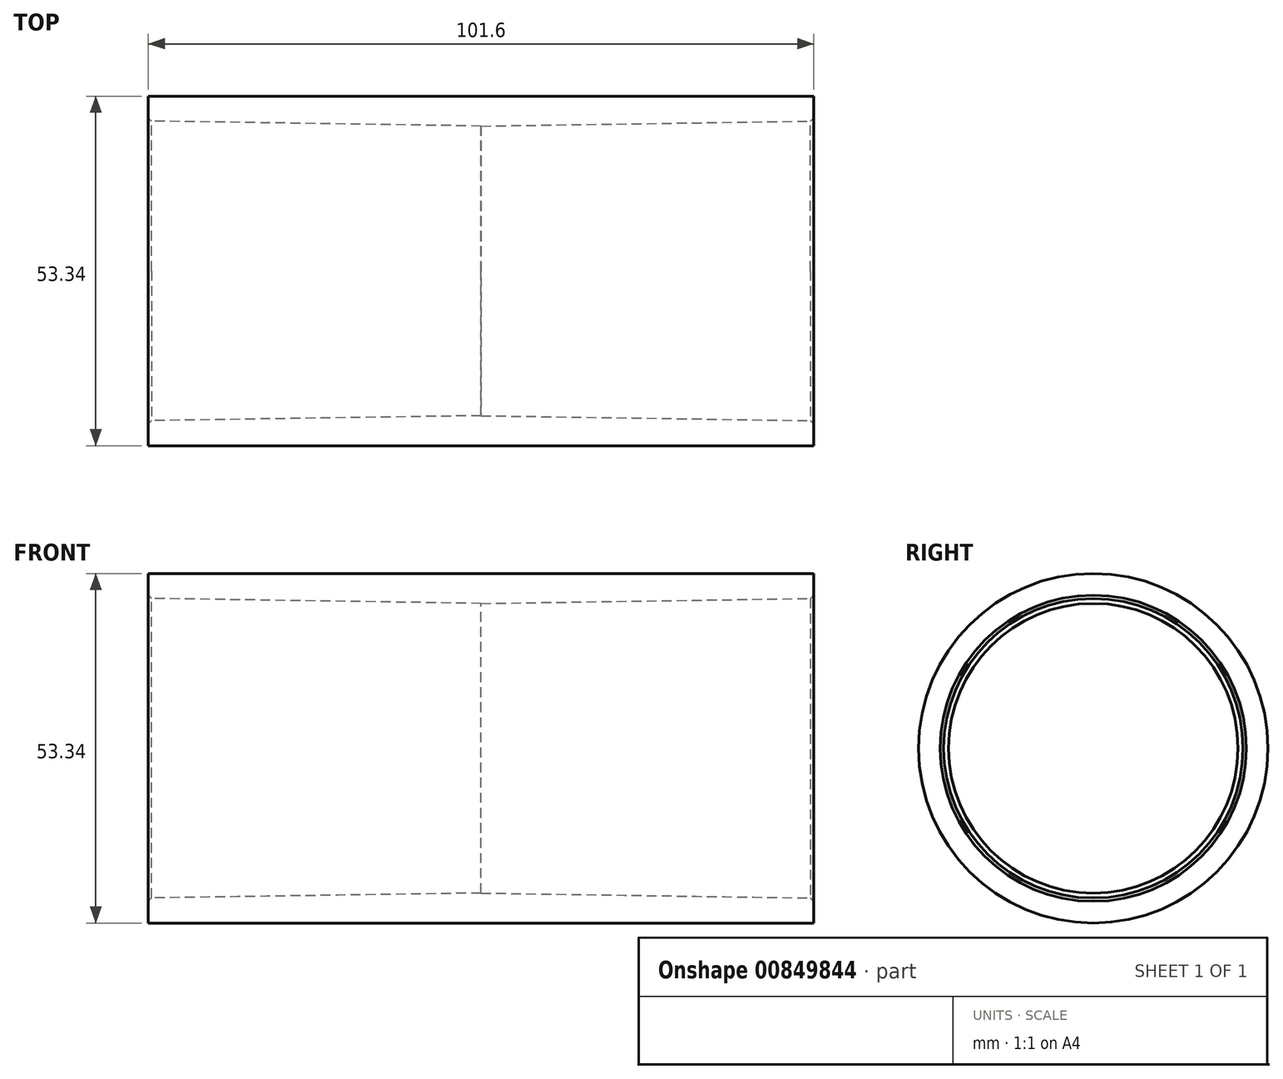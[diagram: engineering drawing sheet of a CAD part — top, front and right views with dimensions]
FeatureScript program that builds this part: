
annotation { "Feature Type Name" : "Feature", "Feature Type Description" : "" }
export const myFeature = defineFeature(function(context is Context, id is Id, definition is map)
    precondition{}
    {
        {
            var Q0;
            Q0=qCreatedBy(makeId("Front.planeOp"),FACE);
            var sketch = newSketch(context, id + "F0", { "sketchPlane" : qUnion([Q0])});
            skLineSegment(sketch, "E0", {"start": v(0, 0) * mm, "end": v(-103.9, 0) * mm, "construction": true});
            skLineSegment(sketch, "E1", {"start": v(0, 26.67) * mm, "end": v(0, 22.1) * mm});
            skLineSegment(sketch, "E2", {"start": v(0, 22.1) * mm, "end": v(50.8, 22.86) * mm});
            skLineSegment(sketch, "E3", {"start": v(50.8, 22.86) * mm, "end": v(50.8, 26.67) * mm});
            skLineSegment(sketch, "E4", {"start": v(50.8, 26.67) * mm, "end": v(0, 26.67) * mm});
            skPoint(sketch, "E5", {"position": v(25.4, 22.48) * mm});
            skSolve(sketch);
        }
        {
            var Q0;
            Q0=qSketchRegion(id+"F0",true);
            var Q1;
            Q1=sQuery(id+"F0.wireOp",EDGE,"E0");
            revolve(context, id + "F1", {"surfaceOperationType" : NewSurfaceOperationType.NEW, "entities" : qUnion([Q0]), "axis" : qUnion([Q1]), "revolveType" : RevolveType.FULL});
        }
        {
            var Q0;
            Q0=makeQuery(id+"F1.opRevolve","SWEPT_BODY",BODY,{"disambiguationData":[OSD([sQuery(id+"F0.wireOp",EDGE,"E1"),sQuery(id+"F0.wireOp",EDGE,"E2"),sQuery(id+"F0.wireOp",EDGE,"E3"),sQuery(id+"F0.wireOp",EDGE,"E4")])]});
            var Q1;
            Q1=makeQuery(id+"F1.opRevolve","SWEPT_FACE",FACE,{"disambiguationData":[OSD([sQuery(id+"F0.wireOp",EDGE,"E1")])]});
            mirror(context, id + "F2", {"operationType" : NewBodyOperationType.ADD, "entities" : qUnion([Q0]), "mirrorPlane" : qUnion([Q1])});
        }
        {
            var Q0;
            Q0=makeQuery(id+"F2.opPattern","COPY",EDGE,{"derivedFrom":makeQuery(id+"F1.opRevolve","SWEPT_EDGE",EDGE,{"disambiguationData":[OSD([sQuery(id+"F0.wireOp",EDGE,"E2"),sQuery(id+"F0.wireOp",EDGE,"E3")])]}),"instanceName":"1"});
            var Q1;
            Q1=makeQuery(id+"F1.opRevolve","SWEPT_EDGE",EDGE,{"disambiguationData":[OSD([sQuery(id+"F0.wireOp",EDGE,"E2"),sQuery(id+"F0.wireOp",EDGE,"E3")])]});
            chamfer(context, id + "F3", {"entities" : qUnion([Q0, Q1]), "width" : 0.5 * mm, "tangentPropagation" : true});
        }
    });
